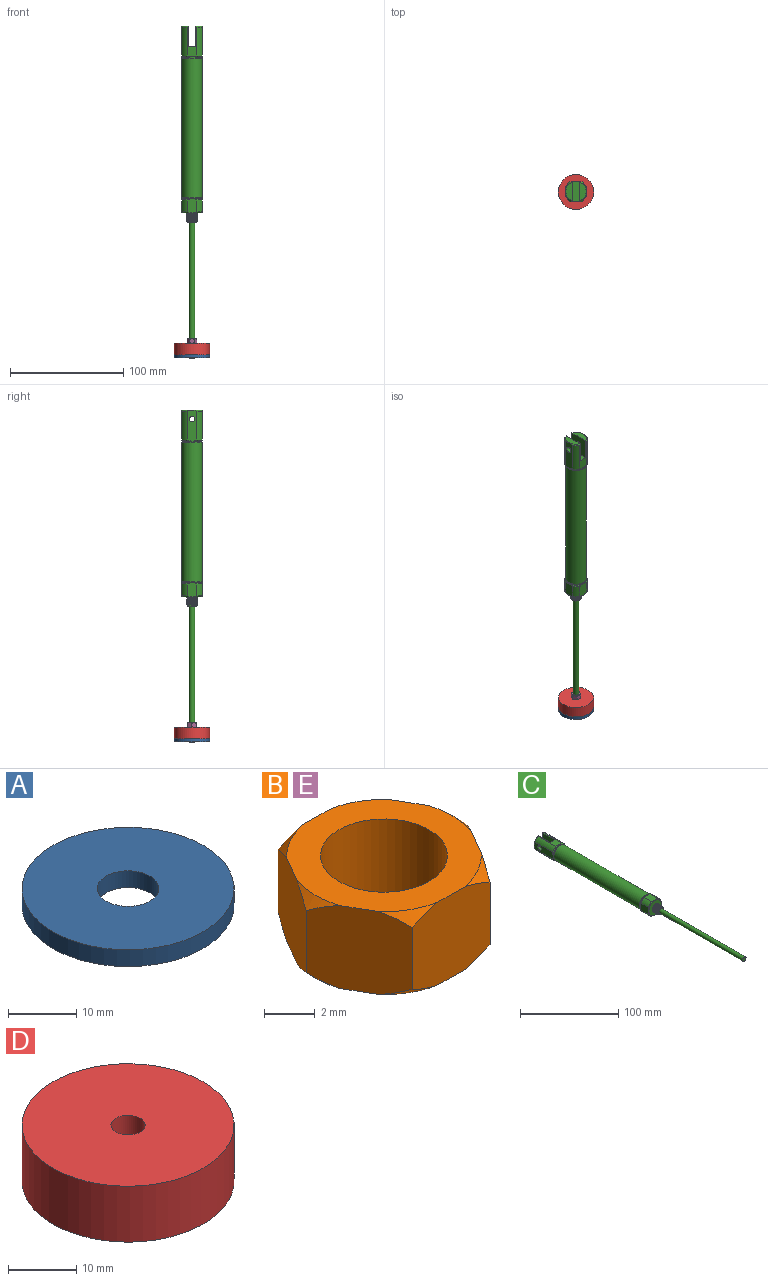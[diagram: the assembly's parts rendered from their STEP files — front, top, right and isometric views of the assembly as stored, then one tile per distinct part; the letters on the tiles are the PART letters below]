
ASSEMBLY  parts=5 mates=4
PART A: 4 faces, bbox 31x31x3 mm
  f0: cylinder r=4.5mm len=9mm, axis (0,0,-1), area 84.8mm2, adj f2,f3
  f1: cylinder r=15.5mm len=31mm, axis (0,0,-1), area 292.2mm2, adj f2,f3
  f2: plane 31x31mm, normal (0,0,1), area 691.2mm2, adj f0,f1
  f3: plane 31x31mm, normal (0,0,-1), area 691.2mm2, adj f0,f1
PART B: 21 faces, bbox 8.8x8.7x4.2 mm
  f0: plane 4.18x3.92mm, normal (0.86,-0.5,0), area 16.1mm2, adj f1,f5,f6,f8,f10,f12,f19,f20
  f1: plane 4.18x3.93mm, normal (0.87,0.5,0), area 16.1mm2, adj f0,f2,f6,f8,f17,f18,f19,f20
  f2: plane 4.5x4.18mm, normal (0,1,0), area 16.1mm2, adj f1,f3,f6,f8,f15,f16,f17,f18
  f3: plane 4.18x3.92mm, normal (-0.86,0.5,0), area 16.1mm2, adj f2,f4,f6,f8,f13,f14,f15,f16
  f4: plane 4.18x3.93mm, normal (-0.87,-0.5,0), area 16.1mm2, adj f3,f5,f6,f8,f9,f11,f13,f14
  f5: plane 4.5x4.18mm, normal (0,-1,0), area 16.1mm2, adj f0,f4,f6,f8,f9,f10,f11,f12
  f6: plane 7.66x7.51mm, normal (0,0,1), area 26mm2, adj f0,f1,f2,f3,f4,f5,f7,f11
  f7: cylinder r=2.5mm len=5mm, axis (0,0,-1), area 62.8mm2, adj f6,f8
  f8: plane 7.66x7.51mm, normal (0,0,-1), area 26mm2, adj f0,f1,f2,f3,f4,f5,f7,f9
  f9: cone r=3.83mm half-angle=45deg, axis (0,0,1), area 0.9mm2, adj f4,f5,f8
  f10: cone r=3.83mm half-angle=45deg, axis (0,0,1), area 0.9mm2, adj f0,f5,f8
  f11: cone r=3.83mm half-angle=45deg, axis (0,0,-1), area 0.9mm2, adj f4,f5,f6
  f12: cone r=3.83mm half-angle=45deg, axis (0,0,-1), area 0.9mm2, adj f0,f5,f6
  f13: cone r=3.83mm half-angle=45deg, axis (0,0,1), area 0.9mm2, adj f3,f4,f8
  f14: cone r=3.83mm half-angle=45deg, axis (0,0,-1), area 0.9mm2, adj f3,f4,f6
  f15: cone r=3.83mm half-angle=45deg, axis (0,0,1), area 0.9mm2, adj f2,f3,f8
  f16: cone r=3.83mm half-angle=45deg, axis (0,0,-1), area 0.9mm2, adj f2,f3,f6
  f17: cone r=3.83mm half-angle=45deg, axis (0,0,1), area 0.9mm2, adj f1,f2,f8
  f18: cone r=3.83mm half-angle=45deg, axis (0,0,-1), area 0.9mm2, adj f1,f2,f6
  f19: cone r=3.83mm half-angle=45deg, axis (0,0,1), area 0.9mm2, adj f0,f1,f8
  f20: cone r=3.83mm half-angle=45deg, axis (0,0,-1), area 0.9mm2, adj f0,f1,f6
PART C: 59 faces, bbox 21x294x21 mm
  f0: plane 16x6.13mm, normal (0,-1,0), area 10.1mm2, adj f4,f41,f42,f57,f58
  f1: cylinder r=9mm len=123mm, axis (0,1,0), area 6955.5mm2, adj f3,f5
  f2: cylinder r=8.5mm len=17mm, axis (0,-1,0), area 53.4mm2, adj f3,f15
  f3: plane 18x18mm, normal (0,-1,0), area 27.5mm2, adj f1,f2
  f4: cylinder r=8.5mm len=17mm, axis (0,1,0), area 54.9mm2, adj f0,f5,f28,f57,f58
  f5: plane 18x18mm, normal (0,1,0), area 27.5mm2, adj f1,f4
  f6: plane 13.22x9.44mm, normal (-1,0,0), area 103mm2, adj f7,f13,f18,f19,f20,f23
  f7: cylinder r=10mm len=10.5mm, axis (0,1,0), area 70.2mm2, adj f6,f8,f19,f20
  f8: plane 13.22x9.44mm, normal (0,0,-1), area 103mm2, adj f7,f9,f17,f19,f20,f21
  f9: cylinder r=10mm len=10.5mm, axis (0,1,0), area 70.2mm2, adj f8,f10,f17,f21
  f10: plane 13.22x9.44mm, normal (1,0,0), area 103mm2, adj f9,f11,f16,f17,f21,f22
  f11: cylinder r=10mm len=10.5mm, axis (0,1,0), area 70.2mm2, adj f10,f12,f16,f22
  f12: plane 13.22x9.44mm, normal (0,0,1), area 103mm2, adj f11,f13,f16,f18,f22,f23
  f13: cylinder r=10mm len=10.5mm, axis (0,1,0), area 70.2mm2, adj f6,f12,f18,f23
  f14: plane 18.46x18.46mm, normal (0,-1,0), area 196.8mm2, adj f20,f21,f22,f23,f25,f52,f53
  f15: plane 18x18mm, normal (0,1,0), area 27.5mm2, adj f2,f16,f17,f18,f19
  f16: cone r=10mm half-angle=45deg, axis (0,-1,0), area 14.9mm2, adj f10,f11,f12,f15
  f17: cone r=10mm half-angle=45deg, axis (0,-1,0), area 14.9mm2, adj f8,f9,f10,f15
  f18: cone r=10mm half-angle=45deg, axis (0,-1,0), area 14.9mm2, adj f6,f12,f13,f15
  f19: cone r=10mm half-angle=45deg, axis (0,-1,0), area 14.9mm2, adj f6,f7,f8,f15
  f20: cone r=9mm half-angle=45deg, axis (0,1,0), area 14.9mm2, adj f6,f7,f8,f14
  f21: cone r=9mm half-angle=45deg, axis (0,1,0), area 14.9mm2, adj f8,f9,f10,f14
  f22: cone r=9mm half-angle=45deg, axis (0,1,0), area 14.9mm2, adj f10,f11,f12,f14
  f23: cone r=9mm half-angle=45deg, axis (0,1,0), area 14.9mm2, adj f6,f12,f13,f14
  f24: cylinder r=2.6mm len=8mm, axis (0,1,0), area 130.7mm2, adj f26,f27
  f25: cylinder r=4mm len=8mm, axis (0,1,0), area 27.1mm2, adj f14,f26,f51,f52,f53
  f26: plane 8x8mm, normal (0,-1,0), area 29mm2, adj f24,f25
  f27: plane 5.2x5.2mm, normal (0,-1,0), area 1.6mm2, adj f24,f54
  f28: plane 16x6.13mm, normal (0,-1,0), area 10.1mm2, adj f4,f43,f44,f57,f58
  f29: plane 28.22x9.44mm, normal (1,0,0), area 214.2mm2, adj f30,f34,f43,f44,f45,f48,f50
  f30: cylinder r=10mm len=25.5mm, axis (0,-1,0), area 170.5mm2, adj f29,f31,f44,f45
  f31: plane 25.98x8.76mm, normal (0,0,-1), area 112.3mm2, adj f30,f32,f36,f37,f45,f46,f56,f58
  f32: plane 18.01x18.01mm, normal (-1,0,0), area 304mm2, adj f31,f33,f35,f45,f48,f50,f56
  f33: plane 25.98x8.76mm, normal (0,0,1), area 112.3mm2, adj f32,f34,f36,f39,f47,f48,f56,f57
  f34: cylinder r=10mm len=25.5mm, axis (0,-1,0), area 170.5mm2, adj f29,f33,f43,f48
  f35: plane 16.79x5.75mm, normal (0,1,0), area 70mm2, adj f32,f45,f48
  f36: plane 18.01x18.01mm, normal (1,0,0), area 304mm2, adj f31,f33,f40,f46,f47,f49,f56
  f37: cylinder r=10mm len=25.5mm, axis (0,-1,0), area 170.5mm2, adj f31,f38,f42,f46
  f38: plane 28.22x9.44mm, normal (-1,0,0), area 214.2mm2, adj f37,f39,f41,f42,f46,f47,f49
  f39: cylinder r=10mm len=25.5mm, axis (0,-1,0), area 170.5mm2, adj f33,f38,f41,f47
  f40: plane 16.79x5.75mm, normal (0,1,0), area 70mm2, adj f36,f46,f47
  f41: cone r=10mm half-angle=45deg, axis (0,1,0), area 11.8mm2, adj f0,f38,f39,f57
  f42: cone r=10mm half-angle=45deg, axis (0,1,0), area 11.8mm2, adj f0,f37,f38,f58
  f43: cone r=10mm half-angle=45deg, axis (0,1,0), area 11.8mm2, adj f28,f29,f34,f57
  f44: cone r=10mm half-angle=45deg, axis (0,1,0), area 11.8mm2, adj f28,f29,f30,f58
  f45: cone r=9mm half-angle=45deg, axis (0,-1,0), area 13mm2, adj f29,f30,f31,f32,f35
  f46: cone r=9mm half-angle=45deg, axis (0,-1,0), area 13mm2, adj f31,f36,f37,f38,f40
  f47: cone r=9mm half-angle=45deg, axis (0,-1,0), area 13mm2, adj f33,f36,f38,f39,f40
  f48: cone r=9mm half-angle=45deg, axis (0,-1,0), area 13mm2, adj f29,f32,f33,f34,f35
  f49: cylinder r=2.5mm len=5.75mm, axis (-1,0,0), area 90.3mm2, adj f36,f38
  f50: cylinder r=2.5mm len=5.75mm, axis (-1,0,0), area 90.3mm2, adj f29,f32
  f51: plane 0.8x0.69mm, normal (0,0,-1), area 0.3mm2, adj f25,f52,f53
  f52: bspline ~10.84x9.39mm, area 161.7mm2, adj f14,f25,f51,f53
  f53: bspline ~10.84x9.39mm, area 171mm2, adj f14,f25,f51,f52
  f54: cylinder r=2.5mm len=128mm, axis (0,1,0), area 2010.6mm2, adj f27,f55
  f55: plane 5x5mm, normal (0,-1,0), area 19.6mm2, adj f54
  f56: plane 18x6.5mm, normal (0,1,0), area 117mm2, adj f31,f32,f33,f36
  f57: plane 8.97x1.25mm, normal (0,-0.71,0.71), area 9.3mm2, adj f0,f4,f28,f33,f41,f43
  f58: plane 9.72x2mm, normal (0,-0.71,-0.71), area 9.3mm2, adj f0,f4,f28,f31,f42,f44
PART D: 6 faces, bbox 31x31x10 mm
  f0: cylinder r=2.5mm len=8mm, axis (0,0,-1), area 125.7mm2, adj f2,f5
  f1: cylinder r=15.5mm len=31mm, axis (0,0,-1), area 973.9mm2, adj f2,f3
  f2: plane 31x31mm, normal (0,0,1), area 735.1mm2, adj f0,f1
  f3: plane 31x31mm, normal (0,0,-1), area 691.2mm2, adj f1,f4
  f4: cylinder r=4.5mm len=9mm, axis (0,0,-1), area 56.5mm2, adj f3,f5
  f5: plane 9x9mm, normal (0,0,-1), area 44mm2, adj f0,f4
PART E: same geometry as B
PLACE A rot(axis=(1,0,0),0deg) t=(-85.96,100.65,-241.49)mm
PLACE B rot(axis=(1,0,0),0deg) t=(-51.43,54.8,-240.49)mm
PLACE C rot(axis=(1,0,0),90deg) t=(-51.43,54.8,-38.49)mm
PLACE D rot(axis=(1,0,0),0deg) t=(-51.43,54.8,-238.49)mm
PLACE E rot(axis=(1,0,0),0deg) t=(-51.43,54.8,-228.49)mm
MATE fastened E.f7 <-> C.f54  axis (0,0,-1) through (-51.43,54.8,-224.49)mm
MATE fastened D.f0 <-> E.f7  axis (0,0,1) through (-51.43,54.8,-228.49)mm
MATE fastened A.f0 <-> D.f1  axis (0,0,1) through (-51.43,54.8,-238.49)mm
MATE fastened B.f7 <-> D.f4  axis (0,0,-1) through (-51.43,54.8,-236.49)mm
